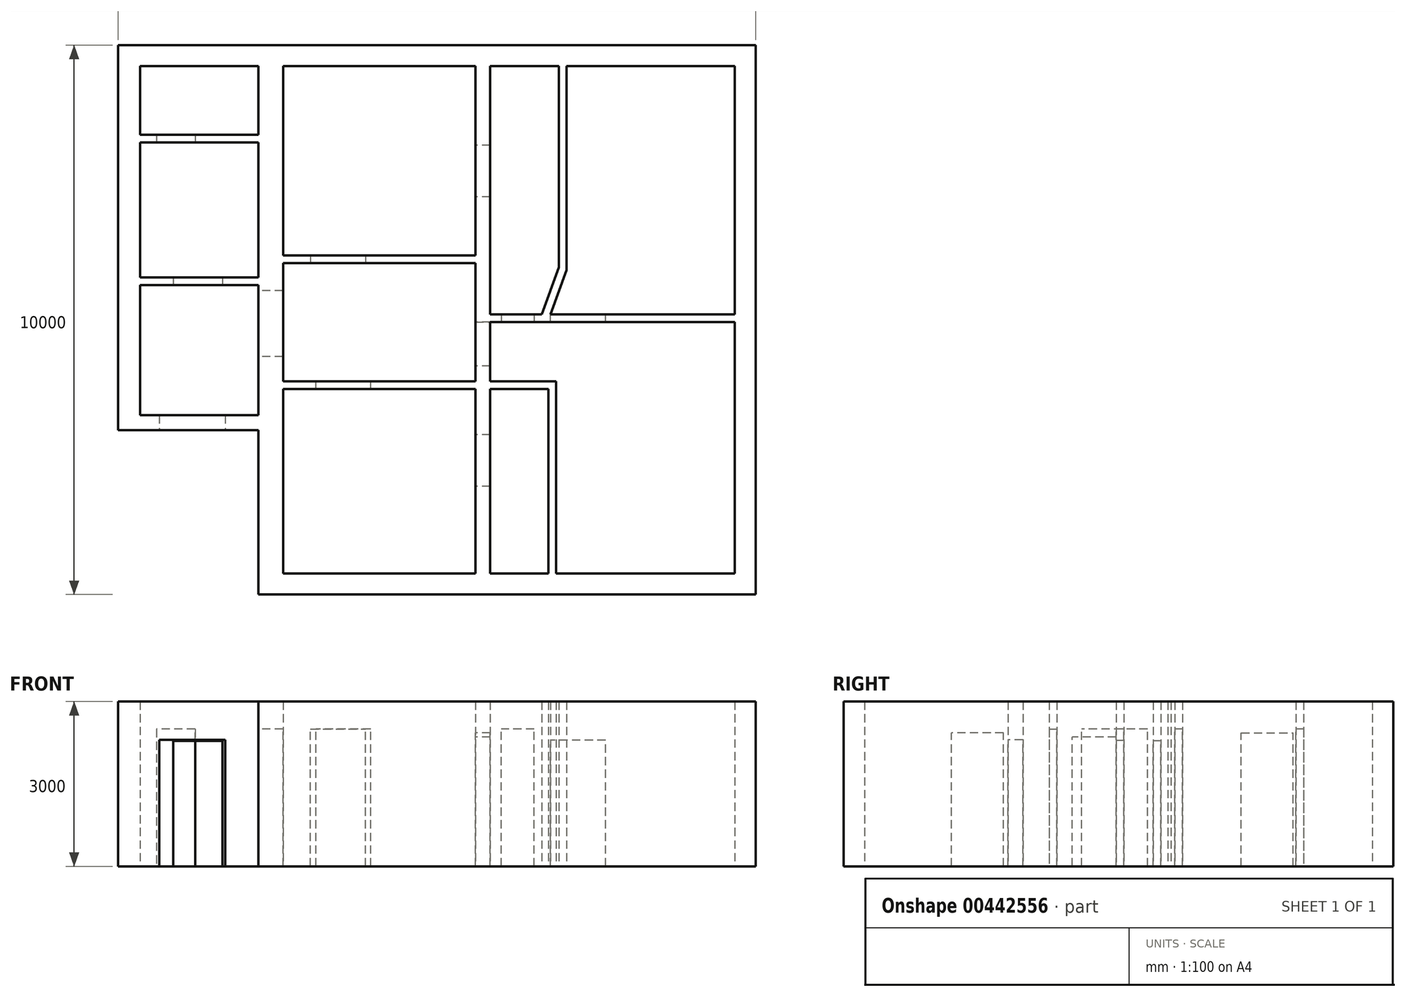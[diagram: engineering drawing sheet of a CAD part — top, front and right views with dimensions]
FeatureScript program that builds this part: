
annotation { "Feature Type Name" : "Feature", "Feature Type Description" : "" }
export const myFeature = defineFeature(function(context is Context, id is Id, definition is map)
    precondition{}
    {
        {
            var Q0;
            Q0=qCreatedBy(makeId("Top.planeOp"),FACE);
            var sketch = newSketch(context, id + "F0", { "sketchPlane" : qUnion([Q0])});
            skLineSegment(sketch, "E0.bottom", {"start": v(-6989.04, 4368.42) * mm, "end": v(4610.96, 4368.42) * mm});
            skLineSegment(sketch, "E0.top", {"start": v(-4439.04, -5631.58) * mm, "end": v(4610.96, -5631.58) * mm});
            skLineSegment(sketch, "E0.left", {"start": v(-6989.04, 4368.42) * mm, "end": v(-6989.04, -2639.49) * mm});
            skLineSegment(sketch, "E0.right", {"start": v(4610.96, 4368.42) * mm, "end": v(4610.96, -5631.58) * mm});
            skLineSegment(sketch, "E1.top", {"start": v(-6989.04, -2639.49) * mm, "end": v(-4439.04, -2639.49) * mm});
            skLineSegment(sketch, "E1.right", {"start": v(-4439.04, -5631.58) * mm, "end": v(-4439.04, -2639.49) * mm});
            skLineSegment(sketch, "E2.bottom", {"start": v(-6589.04, 2598.42) * mm, "end": v(-4439.04, 2598.42) * mm});
            skLineSegment(sketch, "E2.top", {"start": v(-6589.04, 140) * mm, "end": v(-4439.04, 140) * mm});
            skLineSegment(sketch, "E2.left", {"start": v(-6589.04, 2598.42) * mm, "end": v(-6589.04, 140) * mm});
            skLineSegment(sketch, "E2.right", {"start": v(-4439.04, 2598.42) * mm, "end": v(-4439.04, 140) * mm});
            skLineSegment(sketch, "E3.bottom", {"start": v(-6589.04, 0) * mm, "end": v(-4439.04, 0) * mm});
            skLineSegment(sketch, "E3.top", {"start": v(-6589.04, -2369.49) * mm, "end": v(-4439.04, -2369.49) * mm});
            skLineSegment(sketch, "E3.left", {"start": v(-6589.04, 0) * mm, "end": v(-6589.04, -2369.49) * mm});
            skLineSegment(sketch, "E3.right", {"start": v(-4439.04, 0) * mm, "end": v(-4439.04, -2369.49) * mm});
            skLineSegment(sketch, "E4.bottom", {"start": v(-4439.04, 2738.42) * mm, "end": v(-6589.04, 2738.42) * mm});
            skLineSegment(sketch, "E4.top", {"start": v(-4439.04, 3988.42) * mm, "end": v(-6589.04, 3988.42) * mm});
            skLineSegment(sketch, "E4.left", {"start": v(-4439.04, 2738.42) * mm, "end": v(-4439.04, 3988.42) * mm});
            skLineSegment(sketch, "E4.right", {"start": v(-6589.04, 2738.42) * mm, "end": v(-6589.04, 3988.42) * mm});
            skLineSegment(sketch, "E5.bottom", {"start": v(-3989.04, 3988.42) * mm, "end": v(-489.04, 3988.42) * mm});
            skLineSegment(sketch, "E5.top", {"start": v(-3989.04, 538.42) * mm, "end": v(-489.04, 538.42) * mm});
            skLineSegment(sketch, "E5.left", {"start": v(-3989.04, 3988.42) * mm, "end": v(-3989.04, 538.42) * mm});
            skLineSegment(sketch, "E5.right", {"start": v(-489.04, 3988.42) * mm, "end": v(-489.04, 538.42) * mm});
            skLineSegment(sketch, "E6.bottom", {"start": v(-3989.04, -5251.58) * mm, "end": v(-489.04, -5251.58) * mm});
            skLineSegment(sketch, "E6.top", {"start": v(-3989.04, -1891.58) * mm, "end": v(-489.04, -1891.58) * mm});
            skLineSegment(sketch, "E6.left", {"start": v(-3989.04, -5251.58) * mm, "end": v(-3989.04, -1891.58) * mm});
            skLineSegment(sketch, "E6.right", {"start": v(-489.04, -5251.58) * mm, "end": v(-489.04, -1891.58) * mm});
            skLineSegment(sketch, "E7.bottom", {"start": v(-3989.04, 398.42) * mm, "end": v(-489.04, 398.42) * mm});
            skLineSegment(sketch, "E7.top", {"start": v(-3989.04, -1751.58) * mm, "end": v(-489.04, -1751.58) * mm});
            skLineSegment(sketch, "E7.left", {"start": v(-3989.04, 398.42) * mm, "end": v(-3989.04, -1751.58) * mm});
            skLineSegment(sketch, "E7.right", {"start": v(-489.04, 398.42) * mm, "end": v(-489.04, -1751.58) * mm});
            skLineSegment(sketch, "E8.bottom", {"start": v(-219.04, 3988.42) * mm, "end": v(4230.96, 3988.42) * mm});
            skLineSegment(sketch, "E8.top", {"start": v(-219.04, -531.58) * mm, "end": v(4230.96, -531.58) * mm});
            skLineSegment(sketch, "E8.left", {"start": v(-219.04, 3988.42) * mm, "end": v(-219.04, -531.58) * mm});
            skLineSegment(sketch, "E8.right", {"start": v(4230.96, 3988.42) * mm, "end": v(4230.96, -531.58) * mm});
            skLineSegment(sketch, "E9.bottom", {"start": v(-219.04, -671.58) * mm, "end": v(4230.96, -671.58) * mm});
            skLineSegment(sketch, "E9.top", {"start": v(-219.04, -5251.58) * mm, "end": v(4230.96, -5251.58) * mm});
            skLineSegment(sketch, "E9.left", {"start": v(-219.04, -671.58) * mm, "end": v(-219.04, -5251.58) * mm});
            skLineSegment(sketch, "E9.right", {"start": v(4230.96, -671.58) * mm, "end": v(4230.96, -5251.58) * mm});
            skSolve(sketch);
        }
        {
            var Q0;
            Q0 = qSketchRegion(id + "F0", true);
            extrude(context, id + "F1", {"entities" : qUnion([Q0]), "depth" : 3000 * mm});
        }
        {
            var Q0;
            Q0=makeQuery(id+"F1.opExtrude","SWEPT_FACE",FACE,{"disambiguationData":[OSD([sQuery(id+"F0.wireOp",EDGE,"E1.top")])]});
            var sketch = newSketch(context, id + "F2", { "sketchPlane" : qUnion([Q0])});
            skLineSegment(sketch, "E10.bottom", {"start": v(-6239.04, 0) * mm, "end": v(-5039.04, 0) * mm});
            skLineSegment(sketch, "E10.top", {"start": v(-6239.04, 2300) * mm, "end": v(-5039.04, 2300) * mm});
            skLineSegment(sketch, "E10.left", {"start": v(-6239.04, 0) * mm, "end": v(-6239.04, 2300) * mm});
            skLineSegment(sketch, "E10.right", {"start": v(-5039.04, 0) * mm, "end": v(-5039.04, 2300) * mm});
            skSolve(sketch);
        }
        {
            var Q0;
            Q0 = qSketchRegion(id + "F2", true);
            extrude(context, id + "F3", {"entities" : qUnion([Q0]), "operationType" : NewBodyOperationType.REMOVE, "endBound" : BoundingType.UP_TO_NEXT, "oppositeDirection" : true, "depth" : 25 * mm});
        }
        {
            var Q0;
            Q0=makeQuery(id+"F1.opExtrude","SWEPT_FACE",FACE,{"disambiguationData":[OSD([sQuery(id+"F0.wireOp",EDGE,"E3.bottom")])]});
            var sketch = newSketch(context, id + "F4", { "sketchPlane" : qUnion([Q0])});
            skLineSegment(sketch, "E11.bottom", {"start": v(-5989.04, 0) * mm, "end": v(-5089.04, 0) * mm});
            skLineSegment(sketch, "E11.top", {"start": v(-5989.04, 2283.6) * mm, "end": v(-5089.04, 2283.6) * mm});
            skLineSegment(sketch, "E11.left", {"start": v(-5989.04, 0) * mm, "end": v(-5989.04, 2283.6) * mm});
            skLineSegment(sketch, "E11.right", {"start": v(-5089.04, 0) * mm, "end": v(-5089.04, 2283.6) * mm});
            skSolve(sketch);
        }
        {
            var Q0;
            Q0 = qSketchRegion(id + "F4", true);
            extrude(context, id + "F5", {"entities" : qUnion([Q0]), "operationType" : NewBodyOperationType.REMOVE, "endBound" : BoundingType.UP_TO_NEXT, "oppositeDirection" : true, "depth" : 25 * mm});
        }
        {
            var Q0;
            Q0=makeQuery(id+"F1.opExtrude","SWEPT_FACE",FACE,{"disambiguationData":[OSD([sQuery(id+"F0.wireOp",EDGE,"E2.bottom")])]});
            var sketch = newSketch(context, id + "F6", { "sketchPlane" : qUnion([Q0])});
            skLineSegment(sketch, "E12.bottom", {"start": v(-6289.04, 0) * mm, "end": v(-5589.04, 0) * mm});
            skLineSegment(sketch, "E12.top", {"start": v(-6289.04, 2500) * mm, "end": v(-5589.04, 2500) * mm});
            skLineSegment(sketch, "E12.left", {"start": v(-6289.04, 0) * mm, "end": v(-6289.04, 2500) * mm});
            skLineSegment(sketch, "E12.right", {"start": v(-5589.04, 0) * mm, "end": v(-5589.04, 2500) * mm});
            skSolve(sketch);
        }
        {
            var Q0;
            Q0 = qSketchRegion(id + "F6", true);
            extrude(context, id + "F7", {"entities" : qUnion([Q0]), "operationType" : NewBodyOperationType.REMOVE, "endBound" : BoundingType.UP_TO_NEXT, "oppositeDirection" : true, "depth" : 25 * mm});
        }
        {
            var Q0;
            Q0=makeQuery(id+"F1.opExtrude","SWEPT_FACE",FACE,{"disambiguationData":[OSD([sQuery(id+"F0.wireOp",EDGE,"E3.right")])]});
            var sketch = newSketch(context, id + "F8", { "sketchPlane" : qUnion([Q0])});
            skLineSegment(sketch, "E13.bottom", {"start": v(100, 0) * mm, "end": v(1300, 0) * mm});
            skLineSegment(sketch, "E13.top", {"start": v(100, 2500) * mm, "end": v(1300, 2500) * mm});
            skLineSegment(sketch, "E13.left", {"start": v(100, 0) * mm, "end": v(100, 2500) * mm});
            skLineSegment(sketch, "E13.right", {"start": v(1300, 0) * mm, "end": v(1300, 2500) * mm});
            skSolve(sketch);
        }
        {
            var Q0;
            Q0 = qSketchRegion(id + "F8", true);
            extrude(context, id + "F9", {"entities" : qUnion([Q0]), "operationType" : NewBodyOperationType.REMOVE, "endBound" : BoundingType.UP_TO_NEXT, "oppositeDirection" : true, "depth" : 25 * mm});
        }
        {
            var Q0;
            Q0=makeQuery(id+"F1.opExtrude","SWEPT_FACE",FACE,{"disambiguationData":[OSD([sQuery(id+"F0.wireOp",EDGE,"E7.bottom")])]});
            var sketch = newSketch(context, id + "F10", { "sketchPlane" : qUnion([Q0])});
            skLineSegment(sketch, "E14.bottom", {"start": v(-3489.04, 0) * mm, "end": v(-2489.04, 0) * mm});
            skLineSegment(sketch, "E14.top", {"start": v(-3489.04, 2500) * mm, "end": v(-2489.04, 2500) * mm});
            skLineSegment(sketch, "E14.left", {"start": v(-3489.04, 0) * mm, "end": v(-3489.04, 2500) * mm});
            skLineSegment(sketch, "E14.right", {"start": v(-2489.04, 0) * mm, "end": v(-2489.04, 2500) * mm});
            skSolve(sketch);
        }
        {
            var Q0;
            Q0 = qSketchRegion(id + "F10", true);
            extrude(context, id + "F11", {"entities" : qUnion([Q0]), "operationType" : NewBodyOperationType.REMOVE, "endBound" : BoundingType.UP_TO_NEXT, "oppositeDirection" : true, "depth" : 25 * mm});
        }
        {
            var Q0;
            Q0=makeQuery(id+"F1.opExtrude","SWEPT_FACE",FACE,{"disambiguationData":[OSD([sQuery(id+"F0.wireOp",EDGE,"E7.top")])]});
            var sketch = newSketch(context, id + "F12", { "sketchPlane" : qUnion([Q0])});
            skLineSegment(sketch, "E15.bottom", {"start": v(2389.04, 0) * mm, "end": v(3389.04, 0) * mm});
            skLineSegment(sketch, "E15.top", {"start": v(2389.04, 2500) * mm, "end": v(3389.04, 2500) * mm});
            skLineSegment(sketch, "E15.left", {"start": v(2389.04, 0) * mm, "end": v(2389.04, 2500) * mm});
            skLineSegment(sketch, "E15.right", {"start": v(3389.04, 0) * mm, "end": v(3389.04, 2500) * mm});
            skSolve(sketch);
        }
        {
            var Q0;
            Q0 = qSketchRegion(id + "F12", true);
            extrude(context, id + "F13", {"entities" : qUnion([Q0]), "operationType" : NewBodyOperationType.REMOVE, "endBound" : BoundingType.UP_TO_NEXT, "oppositeDirection" : true, "depth" : 25 * mm});
        }
        {
            var Q0;
            Q0=makeQuery(id+"F1.opExtrude","SWEPT_FACE",FACE,{"disambiguationData":[OSD([sQuery(id+"F0.wireOp",EDGE,"E8.top")])]});
            var sketch = newSketch(context, id + "F14", { "sketchPlane" : qUnion([Q0])});
            skLineSegment(sketch, "E16.bottom", {"start": v(-1880.96, 0) * mm, "end": v(-880.96, 0) * mm});
            skLineSegment(sketch, "E16.top", {"start": v(-1880.96, 2296.22) * mm, "end": v(-880.96, 2296.22) * mm});
            skLineSegment(sketch, "E16.left", {"start": v(-1880.96, 0) * mm, "end": v(-1880.96, 2296.22) * mm});
            skLineSegment(sketch, "E16.right", {"start": v(-880.96, 0) * mm, "end": v(-880.96, 2296.22) * mm});
            skSolve(sketch);
        }
        {
            var Q0;
            Q0 = qSketchRegion(id + "F14", true);
            extrude(context, id + "F15", {"entities" : qUnion([Q0]), "operationType" : NewBodyOperationType.REMOVE, "endBound" : BoundingType.UP_TO_NEXT, "oppositeDirection" : true, "depth" : 25 * mm});
        }
        {
            var Q0;
            Q0=makeQuery(id+"F1.opExtrude","SWEPT_FACE",FACE,{"disambiguationData":[OSD([sQuery(id+"F0.wireOp",EDGE,"E6.right")])]});
            var sketch = newSketch(context, id + "F16", { "sketchPlane" : qUnion([Q0])});
            skLineSegment(sketch, "E17.bottom", {"start": v(2723.32, 0) * mm, "end": v(3665.45, 0) * mm});
            skLineSegment(sketch, "E17.top", {"start": v(2723.32, 2427.24) * mm, "end": v(3665.45, 2427.24) * mm});
            skLineSegment(sketch, "E17.left", {"start": v(2723.32, 0) * mm, "end": v(2723.32, 2427.24) * mm});
            skLineSegment(sketch, "E17.right", {"start": v(3665.45, 0) * mm, "end": v(3665.45, 2427.24) * mm});
            skLineSegment(sketch, "E18.bottom", {"start": v(-1605.07, 0) * mm, "end": v(-2547.2, 0) * mm});
            skLineSegment(sketch, "E18.top", {"start": v(-1605.07, 2427.24) * mm, "end": v(-2547.2, 2427.24) * mm});
            skLineSegment(sketch, "E18.left", {"start": v(-1605.07, 0) * mm, "end": v(-1605.07, 2427.24) * mm});
            skLineSegment(sketch, "E18.right", {"start": v(-2547.2, 0) * mm, "end": v(-2547.2, 2427.24) * mm});
            skSolve(sketch);
        }
        {
            var Q0;
            Q0 = qSketchRegion(id + "F16", true);
            extrude(context, id + "F17", {"entities" : qUnion([Q0]), "operationType" : NewBodyOperationType.REMOVE, "endBound" : BoundingType.UP_TO_NEXT, "oppositeDirection" : true, "depth" : 25 * mm});
        }
        {
            var Q0;
            Q0=makeQuery(id+"F1.opExtrude","SWEPT_FACE",FACE,{"disambiguationData":[OSD([sQuery(id+"F0.wireOp",EDGE,"E7.right")])]});
            var sketch = newSketch(context, id + "F18", { "sketchPlane" : qUnion([Q0])});
            skLineSegment(sketch, "E19.bottom", {"start": v(671.58, 0) * mm, "end": v(1471.58, 0) * mm});
            skLineSegment(sketch, "E19.top", {"start": v(671.58, 2353.11) * mm, "end": v(1471.58, 2353.11) * mm});
            skLineSegment(sketch, "E19.left", {"start": v(671.58, 0) * mm, "end": v(671.58, 2353.11) * mm});
            skLineSegment(sketch, "E19.right", {"start": v(1471.58, 0) * mm, "end": v(1471.58, 2353.11) * mm});
            skSolve(sketch);
        }
        {
            var Q0;
            Q0 = qSketchRegion(id + "F18", true);
            extrude(context, id + "F19", {"entities" : qUnion([Q0]), "operationType" : NewBodyOperationType.REMOVE, "endBound" : BoundingType.UP_TO_NEXT, "oppositeDirection" : true, "depth" : 25 * mm});
        }
        {
            var Q0;
            Q0=makeQuery(id+"F19.boolean.opBoolean","MERGE",FACE,{"derivedFrom":[makeQuery(id+"F1.opExtrude","SWEPT_FACE",FACE,{"disambiguationData":[OSD([sQuery(id+"F0.wireOp",EDGE,"E9.bottom")])]}),makeQuery(id+"F19.opExtrude","SWEPT_FACE",FACE,{"disambiguationData":[OSD([sQuery(id+"F18.wireOp",EDGE,"E19.left")])]})]});
            var sketch = newSketch(context, id + "F20", { "sketchPlane" : qUnion([Q0])});
            skLineSegment(sketch, "E20.bottom", {"start": v(580.96, 0) * mm, "end": v(-19.04, 0) * mm});
            skLineSegment(sketch, "E20.top", {"start": v(580.96, 2500) * mm, "end": v(-19.04, 2500) * mm});
            skLineSegment(sketch, "E20.left", {"start": v(580.96, 0) * mm, "end": v(580.96, 2500) * mm});
            skLineSegment(sketch, "E20.right", {"start": v(-19.04, 0) * mm, "end": v(-19.04, 2500) * mm});
            skSolve(sketch);
        }
        {
            var Q0;
            Q0 = qSketchRegion(id + "F20", true);
            extrude(context, id + "F21", {"entities" : qUnion([Q0]), "operationType" : NewBodyOperationType.REMOVE, "endBound" : BoundingType.UP_TO_NEXT, "oppositeDirection" : true, "depth" : 25 * mm});
        }
        {
            var Q0;
            {var subQ0=sQuery(id+"F0.wireOp",EDGE,"E6.bottom");var subQ1=sQuery(id+"F0.wireOp",EDGE,"E9.right");var subQ2=sQuery(id+"F0.wireOp",EDGE,"E9.left");var subQ3=sQuery(id+"F0.wireOp",EDGE,"E9.top");var subQ4=sQuery(id+"F0.wireOp",EDGE,"E9.bottom");var subQ5=sQuery(id+"F0.wireOp",EDGE,"E8.right");var subQ6=sQuery(id+"F0.wireOp",EDGE,"E8.left");var subQ7=sQuery(id+"F0.wireOp",EDGE,"E8.top");var subQ8=sQuery(id+"F0.wireOp",EDGE,"E8.bottom");var subQ9=sQuery(id+"F0.wireOp",EDGE,"E7.left");var subQ10=sQuery(id+"F0.wireOp",EDGE,"E7.top");var subQ11=sQuery(id+"F0.wireOp",EDGE,"E7.bottom");var subQ12=sQuery(id+"F0.wireOp",EDGE,"E6.right");var subQ13=sQuery(id+"F0.wireOp",EDGE,"E6.left");var subQ14=sQuery(id+"F0.wireOp",EDGE,"E0.bottom");var subQ15=sQuery(id+"F0.wireOp",EDGE,"E6.top");var subQ16=sQuery(id+"F0.wireOp",EDGE,"E2.left");var subQ17=sQuery(id+"F0.wireOp",EDGE,"E2.top");var subQ18=sQuery(id+"F0.wireOp",EDGE,"E2.bottom");var subQ19=sQuery(id+"F0.wireOp",EDGE,"E1.right");var subQ20=sQuery(id+"F0.wireOp",EDGE,"E1.top");var subQ21=sQuery(id+"F0.wireOp",EDGE,"E2.right");var subQ22=sQuery(id+"F0.wireOp",EDGE,"E5.right");var subQ23=sQuery(id+"F0.wireOp",EDGE,"E0.right");var subQ24=sQuery(id+"F0.wireOp",EDGE,"E0.top");var subQ25=sQuery(id+"F0.wireOp",EDGE,"E0.left");var subQ26=sQuery(id+"F0.wireOp",EDGE,"E3.bottom");var subQ27=sQuery(id+"F0.wireOp",EDGE,"E3.top");var subQ28=sQuery(id+"F0.wireOp",EDGE,"E3.left");var subQ29=sQuery(id+"F0.wireOp",EDGE,"E3.right");var subQ30=sQuery(id+"F0.wireOp",EDGE,"E4.bottom");var subQ31=sQuery(id+"F0.wireOp",EDGE,"E4.top");var subQ32=sQuery(id+"F0.wireOp",EDGE,"E4.left");var subQ33=sQuery(id+"F0.wireOp",EDGE,"E4.right");var subQ34=sQuery(id+"F0.wireOp",EDGE,"E5.bottom");var subQ35=sQuery(id+"F0.wireOp",EDGE,"E5.top");var subQ36=sQuery(id+"F0.wireOp",EDGE,"E5.left");Q0=makeQuery(id+"F17.boolean.opBoolean","SPLIT",FACE,{"disambiguationData":[TD([makeQuery(id+"F1.opExtrude","SWEPT_FACE",FACE,{"disambiguationData":[OSD([subQ14])]})])],"derivedFrom":makeQuery(id+"F1.opExtrude","CAP_FACE",FACE,{"disambiguationData":[OSD([subQ14,subQ24,subQ25,subQ23,subQ20,subQ19,subQ18,subQ17,subQ16,subQ21,subQ26,subQ27,subQ28,subQ29,subQ30,subQ31,subQ32,subQ33,subQ34,subQ35,subQ36,subQ22,subQ0,subQ15,subQ13,subQ12,subQ11,subQ10,subQ9,sQuery(id+"F0.wireOp",EDGE,"E7.right"),subQ8,subQ7,subQ6,subQ5,subQ4,subQ3,subQ2,subQ1])],"isStart":true})});}
            var sketch = newSketch(context, id + "F22", { "sketchPlane" : qUnion([Q0])});
            skLineSegment(sketch, "E21.top", {"start": v(1170.96, -3988.42) * mm, "end": v(1030.96, -3988.42) * mm});
            skLineSegment(sketch, "E21.left", {"start": v(1170.96, -271.58) * mm, "end": v(1170.96, -3988.42) * mm});
            skLineSegment(sketch, "E22", {"start": v(878.64, 531.58) * mm, "end": v(719, 531.58) * mm});
            skLineSegment(sketch, "E23", {"start": v(719, 531.58) * mm, "end": v(1030.96, -325.5) * mm});
            skLineSegment(sketch, "E24", {"start": v(1170.96, -271.58) * mm, "end": v(878.64, 531.58) * mm});
            skLineSegment(sketch, "E25.trimOffspring", {"start": v(1030.96, -325.5) * mm, "end": v(1030.96, -3988.42) * mm});
            skSolve(sketch);
        }
        {
            var Q0;
            Q0 = qSketchRegion(id + "F22", true);
            var Q1;
            Q1=makeQuery(id+"F1.opExtrude","CAP_FACE",FACE,{"disambiguationData":[OSD([sQuery(id+"F0.wireOp",EDGE,"E0.bottom"),sQuery(id+"F0.wireOp",EDGE,"E0.top"),sQuery(id+"F0.wireOp",EDGE,"E0.left"),sQuery(id+"F0.wireOp",EDGE,"E0.right"),sQuery(id+"F0.wireOp",EDGE,"E1.top"),sQuery(id+"F0.wireOp",EDGE,"E1.right"),sQuery(id+"F0.wireOp",EDGE,"E2.bottom"),sQuery(id+"F0.wireOp",EDGE,"E2.top"),sQuery(id+"F0.wireOp",EDGE,"E2.left"),sQuery(id+"F0.wireOp",EDGE,"E2.right"),sQuery(id+"F0.wireOp",EDGE,"E3.bottom"),sQuery(id+"F0.wireOp",EDGE,"E3.top"),sQuery(id+"F0.wireOp",EDGE,"E3.left"),sQuery(id+"F0.wireOp",EDGE,"E3.right"),sQuery(id+"F0.wireOp",EDGE,"E4.bottom"),sQuery(id+"F0.wireOp",EDGE,"E4.top"),sQuery(id+"F0.wireOp",EDGE,"E4.left"),sQuery(id+"F0.wireOp",EDGE,"E4.right"),sQuery(id+"F0.wireOp",EDGE,"E5.bottom"),sQuery(id+"F0.wireOp",EDGE,"E5.top"),sQuery(id+"F0.wireOp",EDGE,"E5.left"),sQuery(id+"F0.wireOp",EDGE,"E5.right"),sQuery(id+"F0.wireOp",EDGE,"E6.bottom"),sQuery(id+"F0.wireOp",EDGE,"E6.top"),sQuery(id+"F0.wireOp",EDGE,"E6.left"),sQuery(id+"F0.wireOp",EDGE,"E6.right"),sQuery(id+"F0.wireOp",EDGE,"E7.bottom"),sQuery(id+"F0.wireOp",EDGE,"E7.top"),sQuery(id+"F0.wireOp",EDGE,"E7.left"),sQuery(id+"F0.wireOp",EDGE,"E7.right"),sQuery(id+"F0.wireOp",EDGE,"E8.bottom"),sQuery(id+"F0.wireOp",EDGE,"E8.top"),sQuery(id+"F0.wireOp",EDGE,"E8.left"),sQuery(id+"F0.wireOp",EDGE,"E8.right"),sQuery(id+"F0.wireOp",EDGE,"E9.bottom"),sQuery(id+"F0.wireOp",EDGE,"E9.top"),sQuery(id+"F0.wireOp",EDGE,"E9.left"),sQuery(id+"F0.wireOp",EDGE,"E9.right")])],"isStart":false});
            extrude(context, id + "F23", {"entities" : qUnion([Q0]), "operationType" : NewBodyOperationType.ADD, "endBound" : BoundingType.UP_TO_SURFACE, "oppositeDirection" : true, "endBoundEntityFace" : qUnion([Q1]), "depth" : 25 * mm});
        }
        {
            var Q0;
            {var subQ0=sQuery(id+"F0.wireOp",EDGE,"E7.right");var subQ1=makeQuery(id+"F1.opExtrude","SWEPT_FACE",FACE,{"disambiguationData":[OSD([subQ0])]});var subQ3=sQuery(id+"F0.wireOp",EDGE,"E7.top");var subQ5=sQuery(id+"F0.wireOp",EDGE,"E6.right");var subQ7=sQuery(id+"F0.wireOp",EDGE,"E9.left");var subQ9=sQuery(id+"F0.wireOp",EDGE,"E6.top");var subQ10=makeQuery(id+"F1.opExtrude","SWEPT_FACE",FACE,{"disambiguationData":[OSD([subQ9])]});var subQ12=sQuery(id+"F0.wireOp",EDGE,"E8.top");var subQ13=sQuery(id+"F0.wireOp",EDGE,"E7.bottom");var subQ14=sQuery(id+"F0.wireOp",EDGE,"E5.top");var subQ15=sQuery(id+"F0.wireOp",EDGE,"E8.left");var subQ16=sQuery(id+"F0.wireOp",EDGE,"E5.right");var subQ17=sQuery(id+"F0.wireOp",EDGE,"E9.bottom");Q0=makeQuery(id+"F19.boolean.opBoolean","SPLIT",FACE,{"disambiguationData":[TD([subQ10])],"derivedFrom":makeQuery(id+"F17.boolean.opBoolean","SPLIT",FACE,{"disambiguationData":[TD([subQ1])],"derivedFrom":makeQuery(id+"F1.opExtrude","CAP_FACE",FACE,{"disambiguationData":[OSD([sQuery(id+"F0.wireOp",EDGE,"E0.bottom"),sQuery(id+"F0.wireOp",EDGE,"E0.top"),sQuery(id+"F0.wireOp",EDGE,"E0.left"),sQuery(id+"F0.wireOp",EDGE,"E0.right"),sQuery(id+"F0.wireOp",EDGE,"E1.top"),sQuery(id+"F0.wireOp",EDGE,"E1.right"),sQuery(id+"F0.wireOp",EDGE,"E2.bottom"),sQuery(id+"F0.wireOp",EDGE,"E2.top"),sQuery(id+"F0.wireOp",EDGE,"E2.left"),sQuery(id+"F0.wireOp",EDGE,"E2.right"),sQuery(id+"F0.wireOp",EDGE,"E3.bottom"),sQuery(id+"F0.wireOp",EDGE,"E3.top"),sQuery(id+"F0.wireOp",EDGE,"E3.left"),sQuery(id+"F0.wireOp",EDGE,"E3.right"),sQuery(id+"F0.wireOp",EDGE,"E4.bottom"),sQuery(id+"F0.wireOp",EDGE,"E4.top"),sQuery(id+"F0.wireOp",EDGE,"E4.left"),sQuery(id+"F0.wireOp",EDGE,"E4.right"),sQuery(id+"F0.wireOp",EDGE,"E5.bottom"),subQ14,sQuery(id+"F0.wireOp",EDGE,"E5.left"),subQ16,sQuery(id+"F0.wireOp",EDGE,"E6.bottom"),subQ9,sQuery(id+"F0.wireOp",EDGE,"E6.left"),subQ5,subQ13,subQ3,sQuery(id+"F0.wireOp",EDGE,"E7.left"),subQ0,sQuery(id+"F0.wireOp",EDGE,"E8.bottom"),subQ12,subQ15,sQuery(id+"F0.wireOp",EDGE,"E8.right"),subQ17,sQuery(id+"F0.wireOp",EDGE,"E9.top"),subQ7,sQuery(id+"F0.wireOp",EDGE,"E9.right")])],"isStart":true})})});}
            var sketch = newSketch(context, id + "F24", { "sketchPlane" : qUnion([Q0])});
            skPoint(sketch, "E26.oppositeSnap0", {"position": v(-1439.04, 1751.58) * mm});
            skLineSegment(sketch, "E26.bottom", {"start": v(-219.04, 1891.58) * mm, "end": v(840.96, 1891.58) * mm});
            skLineSegment(sketch, "E26.top", {"start": v(-219.04, 1751.58) * mm, "end": v(980.96, 1751.58) * mm});
            skLineSegment(sketch, "E26.left", {"start": v(-219.04, 1891.58) * mm, "end": v(-219.04, 1751.58) * mm});
            skLineSegment(sketch, "E27.top", {"start": v(980.96, 5251.58) * mm, "end": v(840.96, 5251.58) * mm});
            skLineSegment(sketch, "E27.left", {"start": v(980.96, 1891.58) * mm, "end": v(980.96, 5251.58) * mm});
            skLineSegment(sketch, "E27.right", {"start": v(840.96, 1891.58) * mm, "end": v(840.96, 5251.58) * mm});
            skLineSegment(sketch, "E28", {"start": v(980.96, 1891.58) * mm, "end": v(980.96, 1751.58) * mm});
            skSolve(sketch);
        }
        {
            var Q0;
            Q0 = qSketchRegion(id + "F24", true);
            var Q1;
            {var subQ0=sQuery(id+"F0.wireOp",EDGE,"E9.right");var subQ1=sQuery(id+"F0.wireOp",EDGE,"E9.left");var subQ2=sQuery(id+"F0.wireOp",EDGE,"E9.top");var subQ3=sQuery(id+"F0.wireOp",EDGE,"E9.bottom");var subQ4=sQuery(id+"F0.wireOp",EDGE,"E8.right");var subQ5=sQuery(id+"F0.wireOp",EDGE,"E8.left");var subQ6=sQuery(id+"F0.wireOp",EDGE,"E8.top");var subQ7=sQuery(id+"F0.wireOp",EDGE,"E8.bottom");var subQ8=sQuery(id+"F0.wireOp",EDGE,"E7.right");var subQ9=sQuery(id+"F0.wireOp",EDGE,"E7.left");var subQ10=sQuery(id+"F0.wireOp",EDGE,"E7.top");var subQ11=sQuery(id+"F0.wireOp",EDGE,"E7.bottom");var subQ12=sQuery(id+"F0.wireOp",EDGE,"E6.right");var subQ13=sQuery(id+"F0.wireOp",EDGE,"E6.left");var subQ14=sQuery(id+"F0.wireOp",EDGE,"E6.top");var subQ15=sQuery(id+"F0.wireOp",EDGE,"E6.bottom");var subQ16=sQuery(id+"F0.wireOp",EDGE,"E5.right");var subQ17=sQuery(id+"F0.wireOp",EDGE,"E5.left");var subQ18=sQuery(id+"F0.wireOp",EDGE,"E5.top");var subQ19=sQuery(id+"F0.wireOp",EDGE,"E5.bottom");var subQ20=sQuery(id+"F0.wireOp",EDGE,"E4.right");var subQ21=sQuery(id+"F0.wireOp",EDGE,"E4.left");var subQ22=sQuery(id+"F0.wireOp",EDGE,"E4.top");var subQ23=sQuery(id+"F0.wireOp",EDGE,"E4.bottom");var subQ24=sQuery(id+"F0.wireOp",EDGE,"E3.right");var subQ25=sQuery(id+"F0.wireOp",EDGE,"E3.left");var subQ26=sQuery(id+"F0.wireOp",EDGE,"E3.top");var subQ27=sQuery(id+"F0.wireOp",EDGE,"E3.bottom");var subQ28=sQuery(id+"F0.wireOp",EDGE,"E2.right");var subQ29=sQuery(id+"F0.wireOp",EDGE,"E2.left");var subQ30=sQuery(id+"F0.wireOp",EDGE,"E2.top");var subQ31=sQuery(id+"F0.wireOp",EDGE,"E2.bottom");var subQ32=sQuery(id+"F0.wireOp",EDGE,"E1.right");var subQ33=sQuery(id+"F0.wireOp",EDGE,"E1.top");var subQ34=sQuery(id+"F0.wireOp",EDGE,"E0.right");var subQ35=sQuery(id+"F0.wireOp",EDGE,"E0.left");var subQ36=sQuery(id+"F0.wireOp",EDGE,"E0.top");var subQ37=sQuery(id+"F0.wireOp",EDGE,"E0.bottom");Q1=makeQuery(id+"F23.boolean.opBoolean","MERGE",FACE,{"derivedFrom":[makeQuery(id+"F1.opExtrude","CAP_FACE",FACE,{"disambiguationData":[OSD([subQ37,subQ36,subQ35,subQ34,subQ33,subQ32,subQ31,subQ30,subQ29,subQ28,subQ27,subQ26,subQ25,subQ24,subQ23,subQ22,subQ21,subQ20,subQ19,subQ18,subQ17,subQ16,subQ15,subQ14,subQ13,subQ12,subQ11,subQ10,subQ9,subQ8,subQ7,subQ6,subQ5,subQ4,subQ3,subQ2,subQ1,subQ0])],"isStart":false}),makeQuery(id+"F23.opExtrude","CAP_FACE",FACE,{"disambiguationData":[OSD([subQ37,subQ36,subQ35,subQ34,subQ33,subQ32,subQ31,subQ30,subQ29,subQ28,subQ27,subQ26,subQ25,subQ24,subQ23,subQ22,subQ21,subQ20,subQ19,subQ18,subQ17,subQ16,subQ15,subQ14,subQ13,subQ12,subQ11,subQ10,subQ9,subQ8,subQ7,subQ6,subQ5,subQ4,subQ3,subQ2,subQ1,subQ0])],"isStart":false})]});}
            extrude(context, id + "F25", {"entities" : qUnion([Q0]), "operationType" : NewBodyOperationType.ADD, "endBound" : BoundingType.UP_TO_SURFACE, "oppositeDirection" : true, "endBoundEntityFace" : qUnion([Q1]), "depth" : 25 * mm, "offsetDistance" : 25 * mm});
        }
    });
